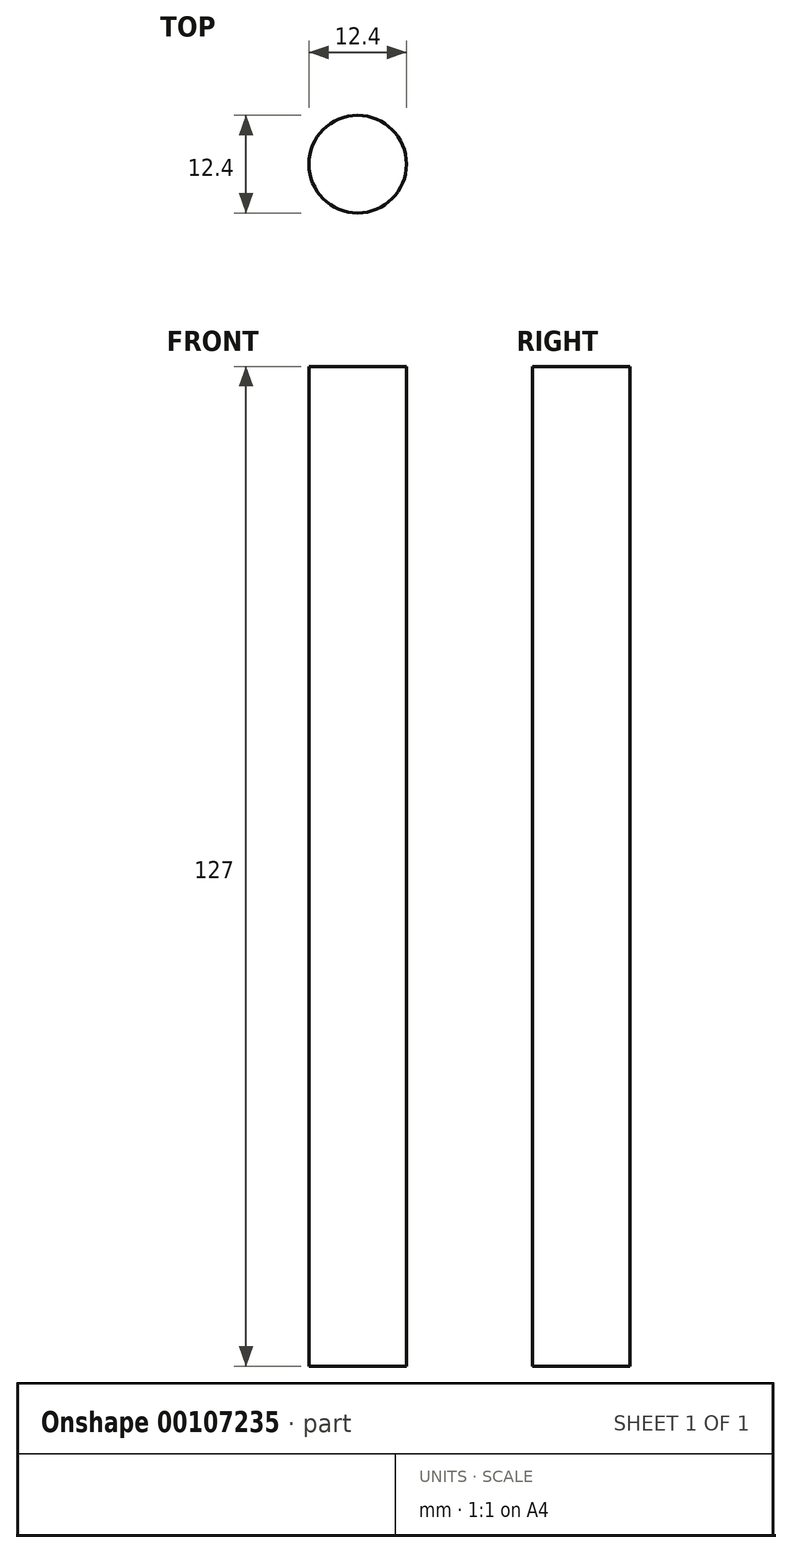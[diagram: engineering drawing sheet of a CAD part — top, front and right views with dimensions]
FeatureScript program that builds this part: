
annotation { "Feature Type Name" : "Feature", "Feature Type Description" : "" }
export const myFeature = defineFeature(function(context is Context, id is Id, definition is map)
    precondition{}
    {
        {
            var Q0;
            Q0=qCreatedBy(makeId("Top.planeOp"),FACE);
            var sketch = newSketch(context, id + "F0", { "sketchPlane" : qUnion([Q0])});
            skCircle(sketch, "E0", {"center": v(0, 0) * mm, "radius": 6.2 * mm});
            skSolve(sketch);
        }
        {
            var Q0;
            Q0=makeQuery(id+"F0.imprint","IMPRINT",FACE,{"disambiguationData":[TD([[makeQuery(id+"F0.imprint","IMPRINT",EDGE,{"derivedFrom":sQuery(id+"F0.wireOp",EDGE,"E0")}),1.0]])]});
            extrude(context, id + "F1", {"entities" : qUnion([Q0]), "depth" : 127 * mm});
        }
    });
